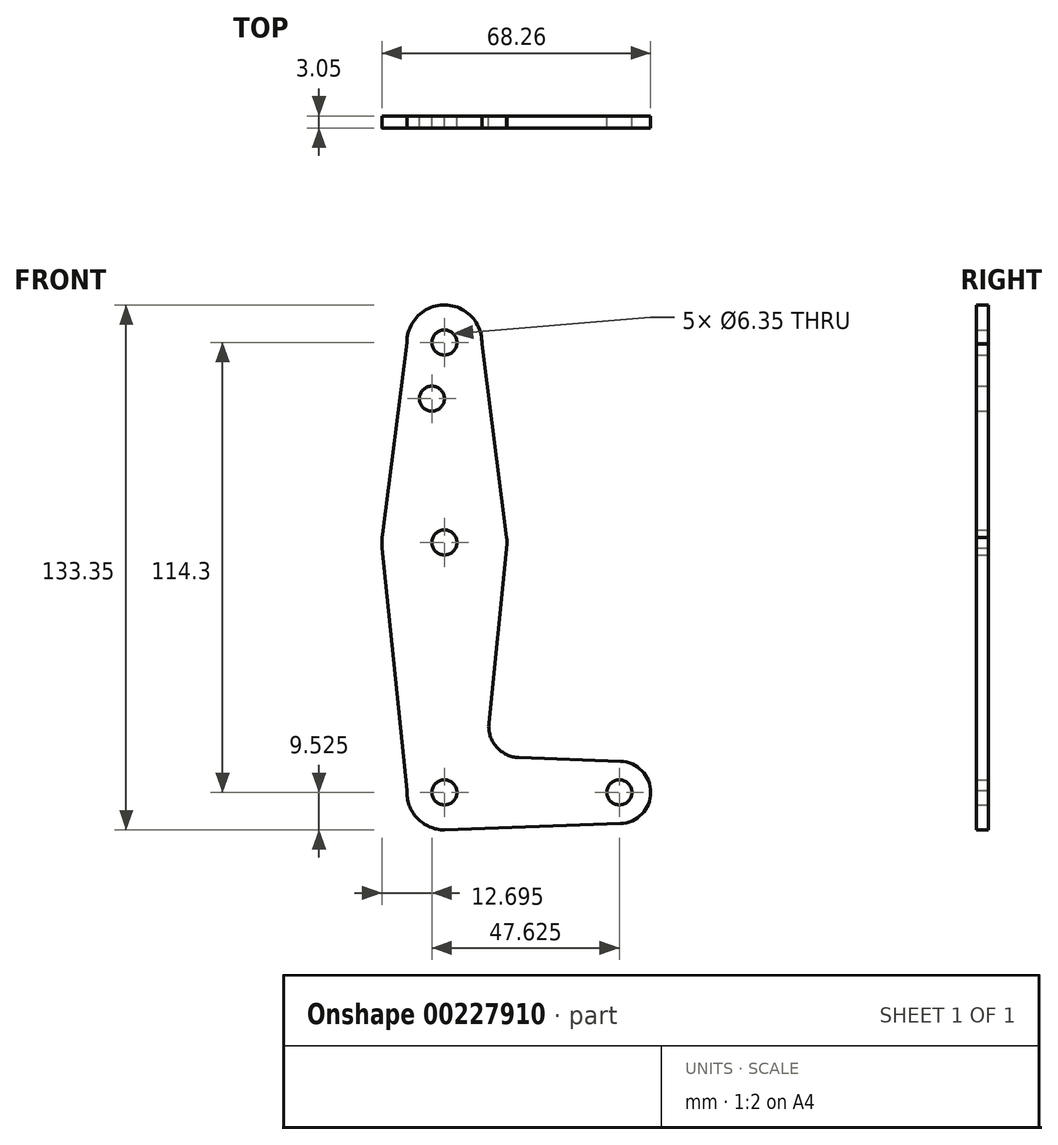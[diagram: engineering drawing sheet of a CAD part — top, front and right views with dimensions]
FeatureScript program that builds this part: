
annotation { "Feature Type Name" : "Feature", "Feature Type Description" : "" }
export const myFeature = defineFeature(function(context is Context, id is Id, definition is map)
    precondition{}
    {
        {
            var Q0;
            Q0=qCreatedBy(makeId("Front.planeOp"),FACE);
            var sketch = newSketch(context, id + "F0", { "sketchPlane" : qUnion([Q0])});
            skLineSegment(sketch, "E0", {"start": v(0, 58.53) * mm, "end": v(0, -55.77) * mm});
            skLineSegment(sketch, "E1", {"start": v(0, -55.77) * mm, "end": v(44.45, -55.77) * mm});
            skCircle(sketch, "E2", {"center": v(0, 58.53) * mm, "radius": 9.53 * mm});
            skCircle(sketch, "E3", {"center": v(0, 7.73) * mm, "radius": 15.88 * mm});
            skCircle(sketch, "E4", {"center": v(0, -55.77) * mm, "radius": 9.53 * mm});
            skCircle(sketch, "E5", {"center": v(44.45, -55.77) * mm, "radius": 7.94 * mm});
            skLineSegment(sketch, "E6", {"start": v(-9.52, 58.56) * mm, "end": v(-15.75, 9.74) * mm});
            skLineSegment(sketch, "E7", {"start": v(-15.8, 6.3) * mm, "end": v(-9.5, -55.21) * mm});
            skLineSegment(sketch, "E8", {"start": v(18.93, -46.91) * mm, "end": v(44.73, -47.83) * mm});
            skLineSegment(sketch, "E9", {"start": v(0, -65.3) * mm, "end": v(44.73, -63.7) * mm});
            skLineSegment(sketch, "E10", {"start": v(11.3, -38.17) * mm, "end": v(15.8, 6.14) * mm});
            skLineSegment(sketch, "E11", {"start": v(15.82, 9) * mm, "end": v(9.52, 58.15) * mm});
            skCircle(sketch, "E12", {"center": v(0, 58.53) * mm, "radius": 3.18 * mm});
            skCircle(sketch, "E13", {"center": v(0, 7.73) * mm, "radius": 3.18 * mm});
            skCircle(sketch, "E14", {"center": v(0, -55.77) * mm, "radius": 3.18 * mm});
            skCircle(sketch, "E15", {"center": v(44.45, -55.77) * mm, "radius": 3.18 * mm});
            skArc(sketch, "E16.filletArc", {"start": v(11.3, -38.17) * mm, "mid": v(13.22, -44.2) * mm, "end": v(18.93, -46.91) * mm});
            skCircle(sketch, "E17", {"center": v(-3.17, 44.26) * mm, "radius": 3.18 * mm});
            skSolve(sketch);
        }
        {
            var Q0;
            {var subQ0=sQuery(id+"F0.wireOp",EDGE,"E11");var subQ1=sQuery(id+"F0.wireOp",EDGE,"E3");var subQ2=makeQuery(id+"F0.imprint","INTERSECT",VERTEX,{"disambiguationData":[OD(0.0)],"derivedFrom":[subQ1,subQ0]});Q0=makeQuery(id+"F0.imprint","IMPRINT",FACE,{"disambiguationData":[TD([[makeQuery(id+"F0.imprint","IMPRINT",EDGE,{"disambiguationData":[TD([[subQ2,-1.0]])],"derivedFrom":subQ1}),1.0]])]});}
            var Q1;
            {var subQ0=sQuery(id+"F0.wireOp",EDGE,"E7");var subQ1=sQuery(id+"F0.wireOp",EDGE,"E3");var subQ2=makeQuery(id+"F0.imprint","INTERSECT",VERTEX,{"disambiguationData":[OD(0.0)],"derivedFrom":[subQ1,subQ0]});Q1=makeQuery(id+"F0.imprint","IMPRINT",FACE,{"disambiguationData":[TD([[makeQuery(id+"F0.imprint","IMPRINT",EDGE,{"disambiguationData":[TD([[subQ2,-1.0]])],"derivedFrom":subQ1}),1.0]])]});}
            var Q2;
            {var subQ0=sQuery(id+"F0.wireOp",EDGE,"E9");var subQ1=sQuery(id+"F0.wireOp",EDGE,"E4");var subQ2=makeQuery(id+"F0.imprint","INTERSECT",VERTEX,{"disambiguationData":[OD(0.0)],"derivedFrom":[subQ1,subQ0]});Q2=makeQuery(id+"F0.imprint","IMPRINT",FACE,{"disambiguationData":[TD([[makeQuery(id+"F0.imprint","IMPRINT",EDGE,{"disambiguationData":[TD([[subQ2,-1.0]])],"derivedFrom":subQ1}),1.0]])]});}
            var Q3;
            {var subQ3=sQuery(id+"F0.wireOp",EDGE,"E0");var subQ8=makeQuery(id+"F0.imprint","INTERSECT",VERTEX,{"derivedFrom":[subQ3,sQuery(id+"F0.wireOp",EDGE,"E17")]});Q3=makeQuery(id+"F0.imprint","IMPRINT",FACE,{"disambiguationData":[TD([[makeQuery(id+"F0.imprint","IMPRINT",EDGE,{"disambiguationData":[TD([[subQ8,1.0]])],"derivedFrom":subQ3}),1.0]])]});}
            var Q4;
            {var subQ0=sQuery(id+"F0.wireOp",EDGE,"E3");var subQ1=sQuery(id+"F0.wireOp",EDGE,"E0");var subQ2=makeQuery(id+"F0.imprint","INTERSECT",VERTEX,{"disambiguationData":[OD(1.0)],"derivedFrom":[subQ1,subQ0]});Q4=makeQuery(id+"F0.imprint","IMPRINT",FACE,{"disambiguationData":[TD([[makeQuery(id+"F0.imprint","IMPRINT",EDGE,{"disambiguationData":[TD([[subQ2,-1.0]])],"derivedFrom":subQ1}),-1.0]])]});}
            var Q5;
            {var subQ0=sQuery(id+"F0.wireOp",EDGE,"E5");var subQ1=sQuery(id+"F0.wireOp",EDGE,"E1");var subQ2=makeQuery(id+"F0.imprint","INTERSECT",VERTEX,{"derivedFrom":[subQ1,subQ0]});Q5=makeQuery(id+"F0.imprint","IMPRINT",FACE,{"disambiguationData":[TD([[makeQuery(id+"F0.imprint","IMPRINT",EDGE,{"disambiguationData":[TD([[subQ2,1.0]])],"derivedFrom":subQ1}),-1.0]])]});}
            var Q6;
            Q6=makeQuery(id+"F0.imprint","IMPRINT",FACE,{"disambiguationData":[TD([[makeQuery(id+"F0.imprint","IMPRINT",EDGE,{"derivedFrom":sQuery(id+"F0.wireOp",EDGE,"E15")}),-1.0]])]});
            var Q7;
            {var subQ0=sQuery(id+"F0.wireOp",EDGE,"E6");Q7=makeQuery(id+"F0.imprint","IMPRINT",FACE,{"disambiguationData":[TD([[makeQuery(id+"F0.imprint","IMPRINT",EDGE,{"derivedFrom":subQ0}),1.0]])]});}
            var Q8;
            {var subQ1=sQuery(id+"F0.wireOp",EDGE,"E3");var subQ3=sQuery(id+"F0.wireOp",EDGE,"E0");var subQ4=makeQuery(id+"F0.imprint","INTERSECT",VERTEX,{"disambiguationData":[OD(0.0)],"derivedFrom":[subQ3,subQ1]});Q8=makeQuery(id+"F0.imprint","IMPRINT",FACE,{"disambiguationData":[TD([[makeQuery(id+"F0.imprint","IMPRINT",EDGE,{"disambiguationData":[TD([[subQ4,-1.0]])],"derivedFrom":subQ3}),1.0]])]});}
            var Q9;
            {var subQ1=sQuery(id+"F0.wireOp",EDGE,"E0");var subQ3=sQuery(id+"F0.wireOp",EDGE,"E3");var subQ9=makeQuery(id+"F0.imprint","INTERSECT",VERTEX,{"disambiguationData":[OD(0.0)],"derivedFrom":[subQ1,subQ3]});Q9=makeQuery(id+"F0.imprint","IMPRINT",FACE,{"disambiguationData":[TD([[makeQuery(id+"F0.imprint","IMPRINT",EDGE,{"disambiguationData":[TD([[subQ9,-1.0]])],"derivedFrom":subQ1}),-1.0]])]});}
            var Q10;
            {var subQ7=sQuery(id+"F0.wireOp",EDGE,"E8");Q10=makeQuery(id+"F0.imprint","IMPRINT",FACE,{"disambiguationData":[TD([[makeQuery(id+"F0.imprint","IMPRINT",EDGE,{"derivedFrom":subQ7}),-1.0]])]});}
            var Q11;
            {var subQ0=sQuery(id+"F0.wireOp",EDGE,"E4");var subQ2=sQuery(id+"F0.wireOp",EDGE,"E0");var subQ3=makeQuery(id+"F0.imprint","INTERSECT",VERTEX,{"derivedFrom":[subQ2,subQ0]});Q11=makeQuery(id+"F0.imprint","IMPRINT",FACE,{"disambiguationData":[TD([[makeQuery(id+"F0.imprint","IMPRINT",EDGE,{"disambiguationData":[TD([[subQ3,-1.0]])],"derivedFrom":subQ2}),-1.0]])]});}
            var Q12;
            Q12=makeQuery(id+"F0.imprint","IMPRINT",FACE,{"disambiguationData":[TD([[makeQuery(id+"F0.imprint","IMPRINT",EDGE,{"derivedFrom":sQuery(id+"F0.wireOp",EDGE,"E12")}),-1.0]])]});
            var Q13;
            {var subQ0=sQuery(id+"F0.wireOp",EDGE,"E4");var subQ1=sQuery(id+"F0.wireOp",EDGE,"E0");var subQ2=makeQuery(id+"F0.imprint","INTERSECT",VERTEX,{"derivedFrom":[subQ1,subQ0]});Q13=makeQuery(id+"F0.imprint","IMPRINT",FACE,{"disambiguationData":[TD([[makeQuery(id+"F0.imprint","IMPRINT",EDGE,{"disambiguationData":[TD([[subQ2,-1.0]])],"derivedFrom":subQ1}),1.0]])]});}
            extrude(context, id + "F1", {"entities" : qUnion([Q0, Q1, Q2, Q3, Q4, Q5, Q6, Q7, Q8, Q9, Q10, Q11, Q12, Q13]), "depth" : 3.05 * mm});
        }
    });
